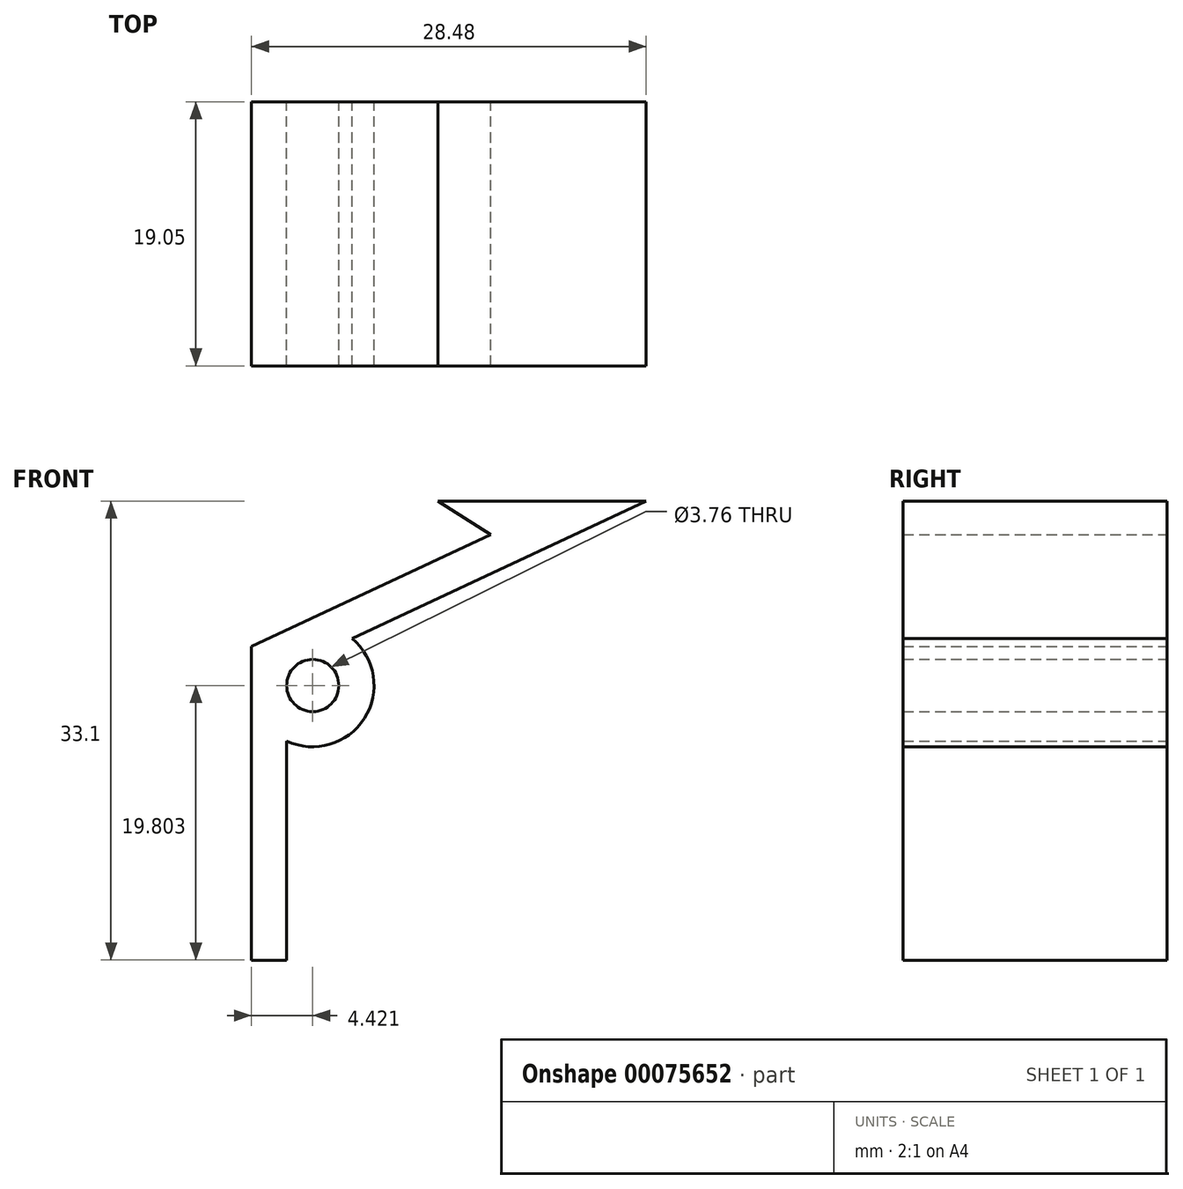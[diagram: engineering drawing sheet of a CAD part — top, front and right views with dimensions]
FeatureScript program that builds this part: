
annotation { "Feature Type Name" : "Feature", "Feature Type Description" : "" }
export const myFeature = defineFeature(function(context is Context, id is Id, definition is map)
    precondition{}
    {
        {
            var Q0;
            Q0=qCreatedBy(makeId("Front.planeOp"),FACE);
            var sketch = newSketch(context, id + "F0", { "sketchPlane" : qUnion([Q0])});
            skLineSegment(sketch, "E0.top", {"start": v(0, -22.62) * mm, "end": v(2.54, -22.62) * mm});
            skLineSegment(sketch, "E0.left", {"start": v(0, 0) * mm, "end": v(0, -22.62) * mm});
            skLineSegment(sketch, "E0.right", {"start": v(2.54, -6.82) * mm, "end": v(2.54, -22.62) * mm});
            skLineSegment(sketch, "E1", {"start": v(0, 0) * mm, "end": v(17.27, 8.05) * mm});
            skLineSegment(sketch, "E2", {"start": v(17.27, 8.05) * mm, "end": v(13.46, 10.48) * mm});
            skLineSegment(sketch, "E3", {"start": v(13.46, 10.48) * mm, "end": v(28.48, 10.48) * mm});
            skLineSegment(sketch, "E4", {"start": v(17.27, 8.05) * mm, "end": v(18.34, 5.75) * mm, "construction": true});
            skLineSegment(sketch, "E5", {"start": v(7.25, 0.58) * mm, "end": v(28.48, 10.48) * mm});
            skCircle(sketch, "E6", {"center": v(4.42, -2.82) * mm, "radius": 1.88 * mm});
            skArc(sketch, "E7", {"start": v(2.54, -6.82) * mm, "mid": v(8.15, -5.2) * mm, "end": v(7.25, 0.58) * mm});
            skSolve(sketch);
        }
        {
            var Q0;
            Q0=makeQuery(id+"F0.imprint","IMPRINT",FACE,{"disambiguationData":[TD([[makeQuery(id+"F0.imprint","IMPRINT",EDGE,{"derivedFrom":sQuery(id+"F0.wireOp",EDGE,"E0.top")}),1.0]])]});
            extrude(context, id + "F1", {"entities" : qUnion([Q0]), "depth" : 19.05 * mm});
        }
    });
